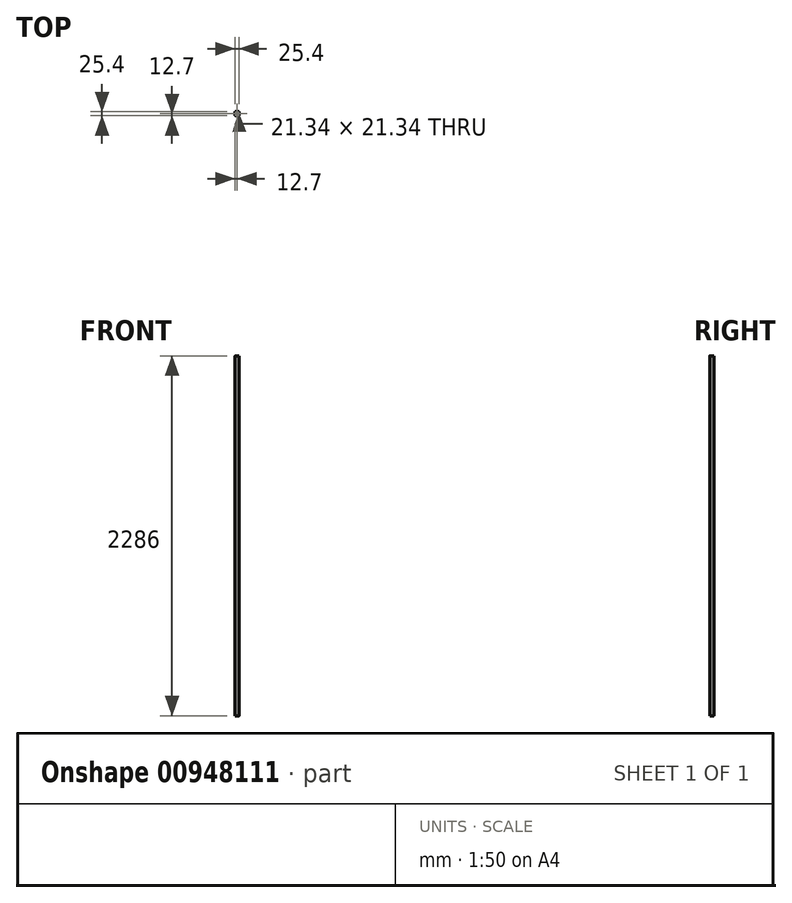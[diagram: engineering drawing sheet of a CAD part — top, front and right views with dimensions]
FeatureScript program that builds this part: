
annotation { "Feature Type Name" : "Feature", "Feature Type Description" : "" }
export const myFeature = defineFeature(function(context is Context, id is Id, definition is map)
    precondition{}
    {
        {
            var Q0;
            Q0=qCreatedBy(makeId("Top.planeOp"),FACE);
            var sketch = newSketch(context, id + "F0", { "sketchPlane" : qUnion([Q0])});
            skLineSegment(sketch, "E0.bottom", {"start": v(12.7, 12.7) * mm, "end": v(-12.7, 12.7) * mm});
            skLineSegment(sketch, "E0.top", {"start": v(12.7, -12.7) * mm, "end": v(-12.7, -12.7) * mm});
            skLineSegment(sketch, "E0.left", {"start": v(12.7, 12.7) * mm, "end": v(12.7, -12.7) * mm});
            skLineSegment(sketch, "E0.right", {"start": v(-12.7, 12.7) * mm, "end": v(-12.7, -12.7) * mm});
            skPoint(sketch, "E0.middle", {"position": v(0, 0) * mm});
            skLineSegment(sketch, "E1.bottom", {"start": v(10.67, 10.67) * mm, "end": v(-10.67, 10.67) * mm});
            skLineSegment(sketch, "E1.top", {"start": v(10.67, -10.67) * mm, "end": v(-10.67, -10.67) * mm});
            skLineSegment(sketch, "E1.left", {"start": v(10.67, 10.67) * mm, "end": v(10.67, -10.67) * mm});
            skLineSegment(sketch, "E1.right", {"start": v(-10.67, 10.67) * mm, "end": v(-10.67, -10.67) * mm});
            skPoint(sketch, "E2.visualSharp", {"position": v(-12.7, 12.7) * mm});
            skLineSegment(sketch, "E2.filletArc", {"start": v(-12.7, 12.7) * mm, "end": v(-12.7, 12.7) * mm});
            skPoint(sketch, "E3.visualSharp", {"position": v(12.7, 12.7) * mm});
            skLineSegment(sketch, "E3.filletArc", {"start": v(12.7, 12.7) * mm, "end": v(12.7, 12.7) * mm});
            skPoint(sketch, "E4.visualSharp", {"position": v(12.7, -12.7) * mm});
            skLineSegment(sketch, "E4.filletArc", {"start": v(12.7, -12.7) * mm, "end": v(12.7, -12.7) * mm});
            skPoint(sketch, "E5.visualSharp", {"position": v(-12.7, -12.7) * mm});
            skLineSegment(sketch, "E5.filletArc", {"start": v(-12.7, -12.7) * mm, "end": v(-12.7, -12.7) * mm});
            skSolve(sketch);
        }
        {
            var Q0;
            Q0=makeQuery(id+"F0.imprint","IMPRINT",FACE,{"disambiguationData":[TD([[makeQuery(id+"F0.imprint","IMPRINT",EDGE,{"derivedFrom":sQuery(id+"F0.wireOp",EDGE,"E0.bottom")}),1.0]])]});
            extrude(context, id + "F1", {"entities" : qUnion([Q0]), "depth" : 2133.6 * mm, "offsetDistance" : 25 * mm});
        }
        {
            var Q0;
            Q0=makeQuery(id+"F1.opExtrude","SWEPT_FACE",FACE,{"disambiguationData":[OSD([sQuery(id+"F0.wireOp",EDGE,"E0.top")])]});
            var sketch = newSketch(context, id + "F2", { "sketchPlane" : qUnion([Q0])});
            skLineSegment(sketch, "E6", {"start": v(0, 0) * mm, "end": v(0, 152.4) * mm, "construction": true});
            skLineSegment(sketch, "E7", {"start": v(-12.7, 152.4) * mm, "end": v(12.7, 152.4) * mm, "construction": true});
            skSolve(sketch);
        }
        {
            var Q0;
            Q0=makeQuery(id+"F1.opExtrude","SWEPT_EDGE",EDGE,{"disambiguationData":[OSD([sQuery(id+"F0.wireOp",EDGE,"E0.bottom"),sQuery(id+"F0.wireOp",EDGE,"E0.right")])]});
            var Q1;
            Q1=makeQuery(id+"F1.opExtrude","SWEPT_EDGE",EDGE,{"disambiguationData":[OSD([sQuery(id+"F0.wireOp",EDGE,"E0.bottom"),sQuery(id+"F0.wireOp",EDGE,"E0.left")])]});
            var Q2;
            Q2=makeQuery(id+"F1.opExtrude","SWEPT_EDGE",EDGE,{"disambiguationData":[OSD([sQuery(id+"F0.wireOp",EDGE,"E0.top"),sQuery(id+"F0.wireOp",EDGE,"E0.left")])]});
            var Q3;
            Q3=makeQuery(id+"F1.opExtrude","SWEPT_EDGE",EDGE,{"disambiguationData":[OSD([sQuery(id+"F0.wireOp",EDGE,"E0.top"),sQuery(id+"F0.wireOp",EDGE,"E0.right")])]});
            fillet(context, id + "F3", {"entities" : qUnion([Q0, Q1, Q2, Q3]), "radius" : 2.5 * mm, "tangentPropagation" : true, "allowEdgeOverflow" : false});
        }
        {
            var Q0;
            Q0=makeQuery(id+"F1.opExtrude","CAP_FACE",FACE,{"disambiguationData":[OSD([sQuery(id+"F0.wireOp",EDGE,"E0.bottom"),sQuery(id+"F0.wireOp",EDGE,"E0.top"),sQuery(id+"F0.wireOp",EDGE,"E0.left"),sQuery(id+"F0.wireOp",EDGE,"E0.right"),sQuery(id+"F0.wireOp",EDGE,"E1.bottom"),sQuery(id+"F0.wireOp",EDGE,"E1.top"),sQuery(id+"F0.wireOp",EDGE,"E1.left"),sQuery(id+"F0.wireOp",EDGE,"E1.right")])],"isStart":true});
            extrude(context, id + "F4", {"entities" : qUnion([Q0]), "operationType" : NewBodyOperationType.ADD, "depth" : 152.4 * mm, "offsetDistance" : 25.4 * mm});
        }
    });
